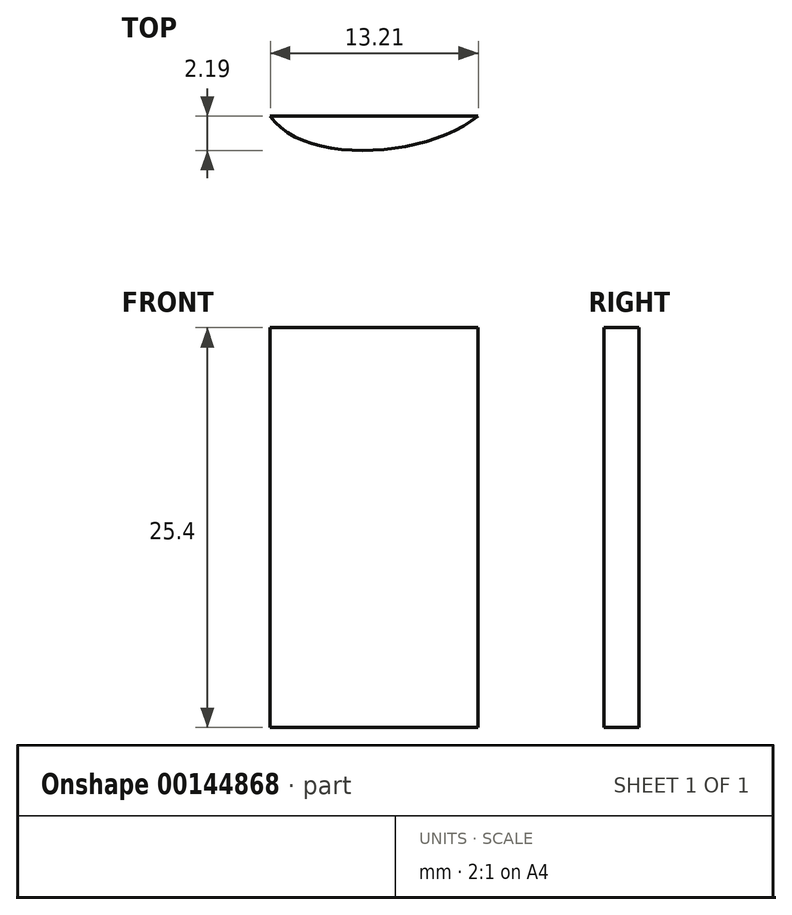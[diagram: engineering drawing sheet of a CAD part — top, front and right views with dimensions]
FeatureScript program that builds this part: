
annotation { "Feature Type Name" : "Feature", "Feature Type Description" : "" }
export const myFeature = defineFeature(function(context is Context, id is Id, definition is map)
    precondition{}
    {
        {
            var Q0;
            Q0=qCreatedBy(makeId("Top.planeOp"),FACE);
            var sketch = newSketch(context, id + "F0", { "sketchPlane" : qUnion([Q0])});
            skFitSpline(sketch, "E0", {"points": [v(-58.17, 9.76) * mm, v(-65.62, 16.6) * mm, v(-67.43, 30.1) * mm, v(-69.64, 24.86) * mm, v(-69.64, 16) * mm, v(-62.6, 0) * mm, v(-63.4, -2.52) * mm, v(-59.18, -6.74) * mm, v(-45.7, -4.33) * mm, v(-31.2, 0) * mm, v(-30.8, -2.52) * mm, v(-31.6, -6.34) * mm, v(-35.02, -11.17) * mm, v(-24.56, -13.79) * mm, v(-21.94, -8.76) * mm, v(-19.73, 0) * mm, v(-16.3, -1.71) * mm, v(-19.32, -18.22) * mm, v(-6.44, -19.02) * mm, v(-3.42, -9.16) * mm, v(-2.62, 0) * mm, v(4.63, 0) * mm, v(3.02, -4.13) * mm, v(0, -8.96) * mm, v(13.08, -10.57) * mm, v(16.3, -0.3) * mm, v(25.97, 0) * mm, v(28.58, 0) * mm, v(28.98, -2.31) * mm, v(28.78, -7.55) * mm, v(29.59, -12.38) * mm, v(28.98, -17.81) * mm, v(41.06, -18.62) * mm, v(43.07, -12.98) * mm, v(44.08, -6.94) * mm, v(43.68, 0) * mm, v(46.7, 11.37) * mm, v(47.7, 8.35) * mm, v(50.52, 5.54) * mm, v(49.92, 10.77) * mm, v(47.7, 18.42) * mm, v(45.49, 31.5) * mm, v(31.2, 41.77) * mm, v(14.09, 43.98) * mm, v(7.85, 42.97) * mm, v(0, 46.2) * mm, v(-20.53, 45.8) * mm, v(-23.75, 45.8) * mm, v(-43.28, 29.69) * mm, v(-47.1, 26.67) * mm, v(-48.3, 25.06) * mm, v(-56.36, 26.87) * mm, v(-55.55, 21.03) * mm, v(-51.73, 20.43) * mm, v(-54.15, 13.59) * mm, v(-59.98, 19.83) * mm, v(-58.17, 9.76) * mm]});
            skLineSegment(sketch, "E1", {"start": v(-50.72, -18.62) * mm, "end": v(57.77, -18.62) * mm});
            skSolve(sketch);
        }
        {
            var Q0;
            {var subQ0=sQuery(id+"F0.wireOp",EDGE,"E1");var subQ1=sQuery(id+"F0.wireOp",EDGE,"E0");var subQ2=makeQuery(id+"F0.imprint","INTERSECT",VERTEX,{"disambiguationData":[OD(2.0)],"derivedFrom":[subQ1,subQ0]});Q0=makeQuery(id+"F0.imprint","IMPRINT",FACE,{"disambiguationData":[TD([[makeQuery(id+"F0.imprint","IMPRINT",EDGE,{"disambiguationData":[TD([[subQ2,-1.0]])],"derivedFrom":subQ1}),1.0]])]});}
            extrude(context, id + "F1", {"entities" : qUnion([Q0]), "depth" : 25.4 * mm});
        }
    });
